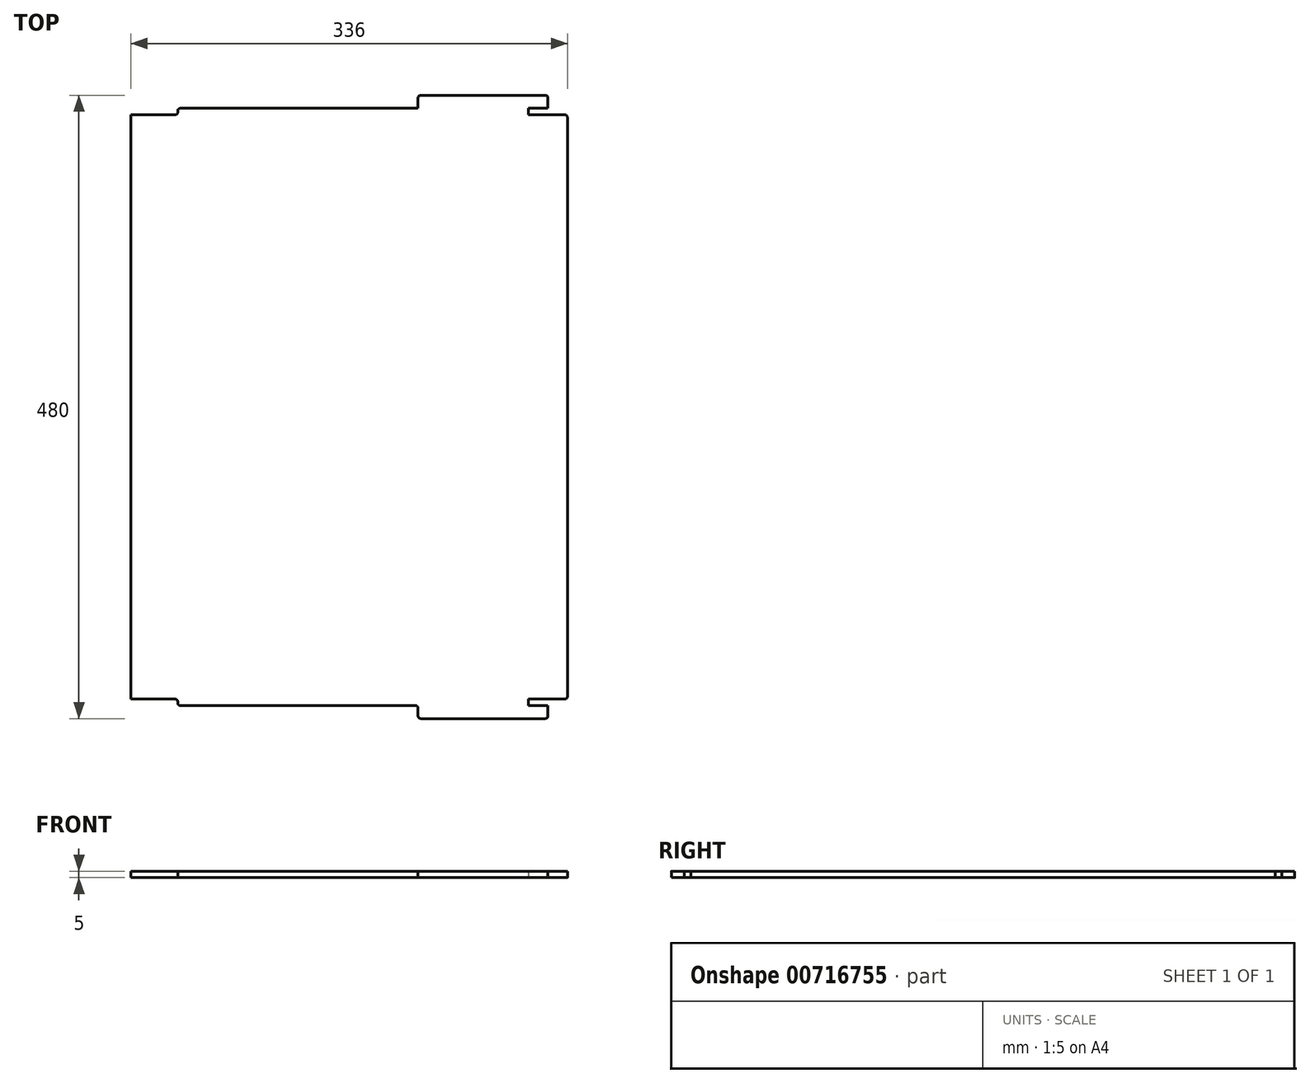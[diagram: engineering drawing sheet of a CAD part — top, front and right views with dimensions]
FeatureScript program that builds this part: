
annotation { "Feature Type Name" : "Feature", "Feature Type Description" : "" }
export const myFeature = defineFeature(function(context is Context, id is Id, definition is map)
    precondition{}
    {
        {
            var Q0;
            Q0=qCreatedBy(makeId("Top.planeOp"),FACE);
            var sketch = newSketch(context, id + "F0", { "sketchPlane" : qUnion([Q0])});
            skLineSegment(sketch, "E0.bottom", {"start": v(173, -225) * mm, "end": v(145, -225) * mm});
            skLineSegment(sketch, "E0.top", {"start": v(173, 225) * mm, "end": v(145, 225) * mm});
            skLineSegment(sketch, "E0.left", {"start": v(175, -223) * mm, "end": v(175, 223) * mm});
            skLineSegment(sketch, "E0.right", {"start": v(-175, -223) * mm, "end": v(-175, 223) * mm});
            skPoint(sketch, "E0.middle", {"position": v(0, 0) * mm});
            skLineSegment(sketch, "E1.top", {"start": v(-123, 230) * mm, "end": v(60, 230) * mm});
            skLineSegment(sketch, "E1.left", {"start": v(-125, 227) * mm, "end": v(-125, 228) * mm});
            skLineSegment(sketch, "E1.right", {"start": v(145, 225) * mm, "end": v(145, 230) * mm});
            skLineSegment(sketch, "E2.trimOffspring", {"start": v(-127, 225) * mm, "end": v(-173, 225) * mm});
            skLineSegment(sketch, "E3.top", {"start": v(-123, -230) * mm, "end": v(58, -230) * mm});
            skLineSegment(sketch, "E3.left", {"start": v(-125, -227) * mm, "end": v(-125, -228) * mm});
            skLineSegment(sketch, "E3.right", {"start": v(145, -225) * mm, "end": v(145, -230) * mm});
            skLineSegment(sketch, "E4.trimOffspring", {"start": v(-127, -225) * mm, "end": v(-173, -225) * mm});
            skLineSegment(sketch, "E5", {"start": v(145, -230) * mm, "end": v(160, -230) * mm});
            skLineSegment(sketch, "E6", {"start": v(160, -230) * mm, "end": v(160, -238) * mm});
            skLineSegment(sketch, "E7", {"start": v(158, -240) * mm, "end": v(62, -240) * mm});
            skLineSegment(sketch, "E8", {"start": v(60, -238) * mm, "end": v(60, -232) * mm});
            skLineSegment(sketch, "E9.MirrorCS", {"start": v(145, 230) * mm, "end": v(160, 230) * mm});
            skLineSegment(sketch, "E10.MirrorCS", {"start": v(160, 230) * mm, "end": v(160, 238) * mm});
            skLineSegment(sketch, "E11.MirrorCS", {"start": v(60, 238) * mm, "end": v(60, 230) * mm});
            skLineSegment(sketch, "E12.MirrorCS", {"start": v(158, 240) * mm, "end": v(62, 240) * mm});
            skPoint(sketch, "E13.visualSharp", {"position": v(60, 240) * mm});
            skArc(sketch, "E13.filletArc", {"start": v(62, 240) * mm, "mid": v(60.59, 239.41) * mm, "end": v(60, 238) * mm});
            skPoint(sketch, "E14.visualSharp", {"position": v(160, 240) * mm});
            skArc(sketch, "E14.filletArc", {"start": v(160, 238) * mm, "mid": v(159.41, 239.41) * mm, "end": v(158, 240) * mm});
            skPoint(sketch, "E15.visualSharp", {"position": v(-125, 230) * mm});
            skArc(sketch, "E15.filletArc", {"start": v(-123, 230) * mm, "mid": v(-124.41, 229.41) * mm, "end": v(-125, 228) * mm});
            skPoint(sketch, "E16.visualSharp", {"position": v(-125, 225) * mm});
            skArc(sketch, "E16.filletArc", {"start": v(-127, 225) * mm, "mid": v(-125.59, 225.59) * mm, "end": v(-125, 227) * mm});
            skPoint(sketch, "E17.visualSharp", {"position": v(-175, 225) * mm});
            skArc(sketch, "E17.filletArc", {"start": v(-173, 225) * mm, "mid": v(-174.41, 224.41) * mm, "end": v(-175, 223) * mm});
            skPoint(sketch, "E18.visualSharp", {"position": v(-175, -225) * mm});
            skArc(sketch, "E18.filletArc", {"start": v(-175, -223) * mm, "mid": v(-174.41, -224.41) * mm, "end": v(-173, -225) * mm});
            skPoint(sketch, "E19.visualSharp", {"position": v(-125, -225) * mm});
            skArc(sketch, "E19.filletArc", {"start": v(-125, -227) * mm, "mid": v(-125.59, -225.59) * mm, "end": v(-127, -225) * mm});
            skPoint(sketch, "E20.visualSharp", {"position": v(-125, -230) * mm});
            skArc(sketch, "E20.filletArc", {"start": v(-125, -228) * mm, "mid": v(-124.41, -229.41) * mm, "end": v(-123, -230) * mm});
            skPoint(sketch, "E21.visualSharp", {"position": v(60, -230) * mm});
            skArc(sketch, "E21.filletArc", {"start": v(60, -232) * mm, "mid": v(59.41, -230.59) * mm, "end": v(58, -230) * mm});
            skPoint(sketch, "E22.visualSharp", {"position": v(60, -240) * mm});
            skArc(sketch, "E22.filletArc", {"start": v(60, -238) * mm, "mid": v(60.59, -239.41) * mm, "end": v(62, -240) * mm});
            skPoint(sketch, "E23.visualSharp", {"position": v(160, -240) * mm});
            skArc(sketch, "E23.filletArc", {"start": v(158, -240) * mm, "mid": v(159.41, -239.41) * mm, "end": v(160, -238) * mm});
            skPoint(sketch, "E24.visualSharp", {"position": v(175, -225) * mm});
            skArc(sketch, "E24.filletArc", {"start": v(173, -225) * mm, "mid": v(174.41, -224.41) * mm, "end": v(175, -223) * mm});
            skPoint(sketch, "E25.visualSharp", {"position": v(175, 225) * mm});
            skArc(sketch, "E25.filletArc", {"start": v(175, 223) * mm, "mid": v(174.41, 224.41) * mm, "end": v(173, 225) * mm});
            skSolve(sketch);
        }
        {
            var Q0;
            Q0=makeQuery(id+"F0.imprint","IMPRINT",FACE,{"disambiguationData":[TD([[makeQuery(id+"F0.imprint","IMPRINT",EDGE,{"derivedFrom":sQuery(id+"F0.wireOp",EDGE,"E0.bottom")}),-1.0]])]});
            extrude(context, id + "F1", {"entities" : qUnion([Q0]), "depth" : 5 * mm, "offsetDistance" : 25 * mm});
        }
        {
            var Q0;
            Q0=makeQuery(id+"F1.opExtrude","CAP_FACE",FACE,{"disambiguationData":[OSD([sQuery(id+"F0.wireOp",EDGE,"E0.bottom"),sQuery(id+"F0.wireOp",EDGE,"E0.top"),sQuery(id+"F0.wireOp",EDGE,"E0.left"),sQuery(id+"F0.wireOp",EDGE,"E0.right"),sQuery(id+"F0.wireOp",EDGE,"E1.top"),sQuery(id+"F0.wireOp",EDGE,"E1.left"),sQuery(id+"F0.wireOp",EDGE,"E1.right"),sQuery(id+"F0.wireOp",EDGE,"E2.trimOffspring"),sQuery(id+"F0.wireOp",EDGE,"E3.top"),sQuery(id+"F0.wireOp",EDGE,"E3.left"),sQuery(id+"F0.wireOp",EDGE,"E3.right"),sQuery(id+"F0.wireOp",EDGE,"E4.trimOffspring"),sQuery(id+"F0.wireOp",EDGE,"E5"),sQuery(id+"F0.wireOp",EDGE,"E6"),sQuery(id+"F0.wireOp",EDGE,"E7"),sQuery(id+"F0.wireOp",EDGE,"E8"),sQuery(id+"F0.wireOp",EDGE,"E9.MirrorCS"),sQuery(id+"F0.wireOp",EDGE,"E10.MirrorCS"),sQuery(id+"F0.wireOp",EDGE,"E11.MirrorCS"),sQuery(id+"F0.wireOp",EDGE,"E12.MirrorCS")])],"isStart":false});
            var sketch = newSketch(context, id + "F2", { "sketchPlane" : qUnion([Q0])});
            skLineSegment(sketch, "E26", {"start": v(-161, 340.58) * mm, "end": v(-161, -338.34) * mm});
            skLineSegment(sketch, "E27", {"start": v(-161, -338.34) * mm, "end": v(-227.95, -338.34) * mm});
            skLineSegment(sketch, "E28", {"start": v(-227.95, -338.34) * mm, "end": v(-227.95, 340.58) * mm});
            skLineSegment(sketch, "E29", {"start": v(-227.95, 340.58) * mm, "end": v(-161, 340.58) * mm});
            skSolve(sketch);
        }
        {
            var Q0;
            {var subQ0=sQuery(id+"F2.wireOp",EDGE,"E27");Q0=makeQuery(id+"F2.imprint","IMPRINT",FACE,{"disambiguationData":[TD([[makeQuery(id+"F2.imprint","IMPRINT",EDGE,{"derivedFrom":subQ0}),-1.0]])]});}
            var Q1;
            {var subQ5=makeQuery(id+"F1.opExtrude","CAP_EDGE",EDGE,{"disambiguationData":[OSD([sQuery(id+"F0.wireOp",EDGE,"E0.right")])],"isStart":false});Q1=makeQuery(id+"F2.imprint","IMPRINT",FACE,{"disambiguationData":[TD([[makeQuery(id+"F2.imprint","IMPRINT",EDGE,{"derivedFrom":subQ5}),-1.0]])]});}
            extrude(context, id + "F3", {"entities" : qUnion([Q0, Q1]), "operationType" : NewBodyOperationType.REMOVE, "oppositeDirection" : true, "depth" : 25 * mm, "offsetDistance" : 25 * mm});
        }
    });
